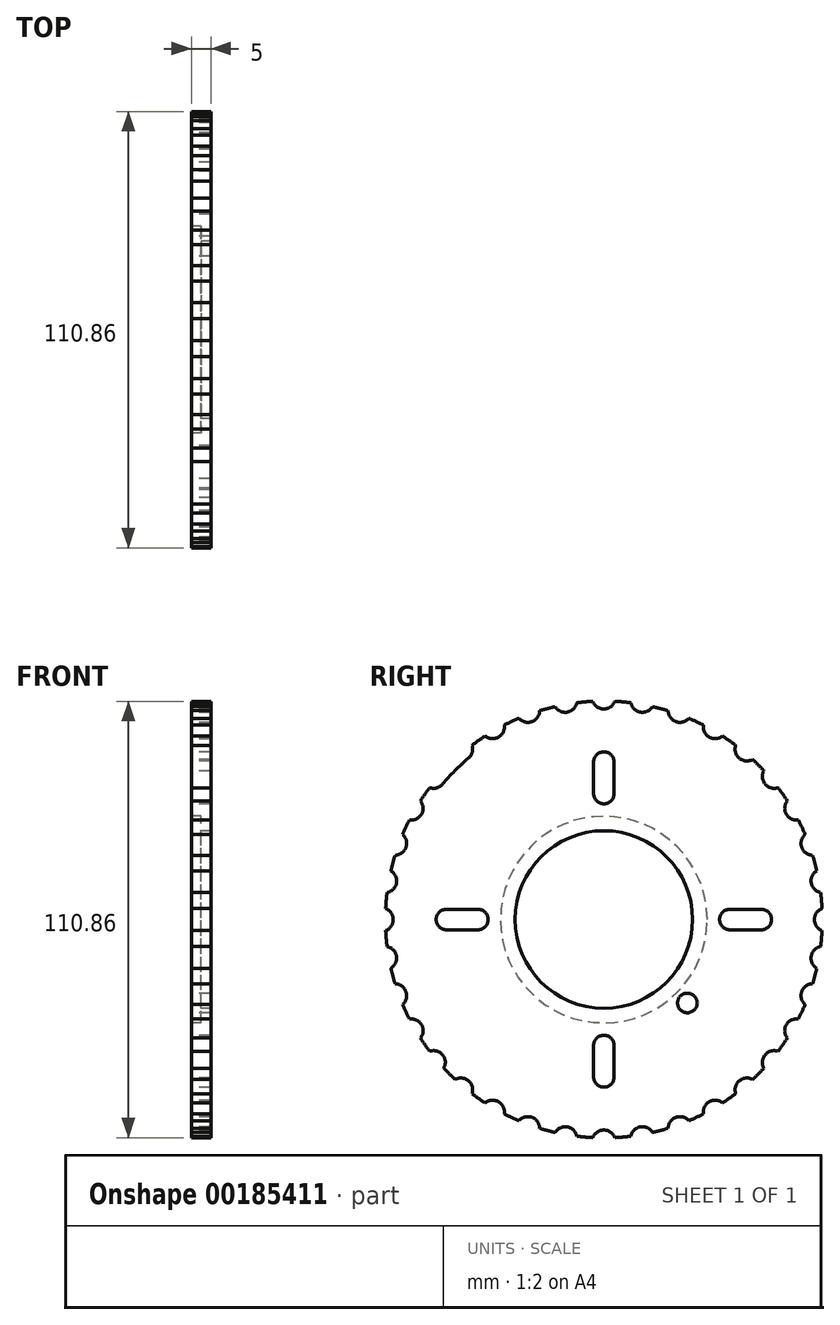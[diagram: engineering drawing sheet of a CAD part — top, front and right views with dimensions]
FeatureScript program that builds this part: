
annotation { "Feature Type Name" : "Feature", "Feature Type Description" : "" }
export const myFeature = defineFeature(function(context is Context, id is Id, definition is map)
    precondition{}
    {
        {
            var Q0;
            Q0=qCreatedBy(makeId("Right.planeOp"),FACE);
            var sketch = newSketch(context, id + "F0", { "sketchPlane" : qUnion([Q0])});
            skCircle(sketch, "E0", {"center": v(0, 0) * mm, "radius": 26.25 * mm});
            skCircle(sketch, "E1", {"center": v(0, 0) * mm, "radius": 22.55 * mm});
            skLineSegment(sketch, "E2", {"start": v(0, 6.12) * mm, "end": v(0, -11) * mm, "construction": true});
            skLineSegment(sketch, "E3", {"start": v(0, 40) * mm, "end": v(0, 32) * mm, "construction": true});
            skArc(sketch, "E4.0.startCap", {"start": v(-2.6, 40) * mm, "mid": v(0, 42.6) * mm, "end": v(2.6, 40) * mm});
            skArc(sketch, "E4.0.endCap", {"start": v(2.6, 32) * mm, "mid": v(0, 29.4) * mm, "end": v(-2.6, 32) * mm});
            skLineSegment(sketch, "E4.0.left", {"start": v(2.6, 40) * mm, "end": v(2.6, 32) * mm});
            skLineSegment(sketch, "E4.0.right", {"start": v(-2.6, 40) * mm, "end": v(-2.6, 32) * mm});
            skArc(sketch, "E5.1.0", {"start": v(-32, 2.6) * mm, "mid": v(-29.4, 0) * mm, "end": v(-32, -2.6) * mm});
            skLineSegment(sketch, "E5.1.1", {"start": v(-40, -2.6) * mm, "end": v(-32, -2.6) * mm});
            skLineSegment(sketch, "E5.1.2", {"start": v(-40, 2.6) * mm, "end": v(-32, 2.6) * mm});
            skArc(sketch, "E5.1.3", {"start": v(-40, -2.6) * mm, "mid": v(-42.6, 0) * mm, "end": v(-40, 2.6) * mm});
            skArc(sketch, "E5.2.0", {"start": v(-2.6, -32) * mm, "mid": v(0, -29.4) * mm, "end": v(2.6, -32) * mm});
            skLineSegment(sketch, "E5.2.1", {"start": v(2.6, -40) * mm, "end": v(2.6, -32) * mm});
            skLineSegment(sketch, "E5.2.2", {"start": v(-2.6, -40) * mm, "end": v(-2.6, -32) * mm});
            skArc(sketch, "E5.2.3", {"start": v(2.6, -40) * mm, "mid": v(0, -42.6) * mm, "end": v(-2.6, -40) * mm});
            skArc(sketch, "E5.3.0", {"start": v(32, -2.6) * mm, "mid": v(29.4, 0) * mm, "end": v(32, 2.6) * mm});
            skLineSegment(sketch, "E5.3.1", {"start": v(40, 2.6) * mm, "end": v(32, 2.6) * mm});
            skLineSegment(sketch, "E5.3.2", {"start": v(40, -2.6) * mm, "end": v(32, -2.6) * mm});
            skArc(sketch, "E5.3.3", {"start": v(40, 2.6) * mm, "mid": v(42.6, 0) * mm, "end": v(40, -2.6) * mm});
            skCircle(sketch, "E6", {"center": v(0, 0) * mm, "radius": 53.5 * mm});
            skArc(sketch, "E7", {"start": v(-2.8, 55.43) * mm, "mid": v(0, -55.5) * mm, "end": v(2.8, 55.43) * mm});
            skCircle(sketch, "E8", {"center": v(0, 0) * mm, "radius": 56.5 * mm, "construction": true});
            skArc(sketch, "E9", {"start": v(-2.8, 55.43) * mm, "mid": v(0, 53.5) * mm, "end": v(2.8, 55.43) * mm});
            skPoint(sketch, "E10.visualSharp", {"position": v(2.8, 55.43) * mm});
            skLineSegment(sketch, "E11", {"start": v(0, 0) * mm, "end": v(21.21, -21.21) * mm, "construction": true});
            skCircle(sketch, "E12", {"center": v(21.21, -21.21) * mm, "radius": 2.5 * mm});
            skArc(sketch, "E13.1.0", {"start": v(-12.38, 54.1) * mm, "mid": v(-9.3, 52.69) * mm, "end": v(-6.87, 55.07) * mm});
            skArc(sketch, "E13.2.0", {"start": v(-21.6, 51.13) * mm, "mid": v(-18.3, 50.27) * mm, "end": v(-16.32, 53.04) * mm});
            skArc(sketch, "E13.3.0", {"start": v(-30.14, 46.6) * mm, "mid": v(-26.75, 46.33) * mm, "end": v(-25.29, 49.4) * mm});
            skArc(sketch, "E13.4.0", {"start": v(-37.78, 40.66) * mm, "mid": v(-34.39, 40.98) * mm, "end": v(-33.48, 44.26) * mm});
            skArc(sketch, "E13.5.0", {"start": v(-44.26, 33.48) * mm, "mid": v(-40.98, 34.39) * mm, "end": v(-40.66, 37.78) * mm});
            skArc(sketch, "E13.6.0", {"start": v(-49.4, 25.29) * mm, "mid": v(-46.33, 26.75) * mm, "end": v(-46.6, 30.14) * mm});
            skArc(sketch, "E13.7.0", {"start": v(-53.04, 16.32) * mm, "mid": v(-50.27, 18.3) * mm, "end": v(-51.13, 21.6) * mm});
            skArc(sketch, "E13.8.0", {"start": v(-55.07, 6.87) * mm, "mid": v(-52.69, 9.3) * mm, "end": v(-54.1, 12.38) * mm});
            skArc(sketch, "E13.9.0", {"start": v(-55.43, -2.8) * mm, "mid": v(-53.5, 0) * mm, "end": v(-55.43, 2.8) * mm});
            skArc(sketch, "E13.10.0", {"start": v(-54.1, -12.38) * mm, "mid": v(-52.69, -9.3) * mm, "end": v(-55.07, -6.87) * mm});
            skArc(sketch, "E13.11.0", {"start": v(-51.13, -21.6) * mm, "mid": v(-50.27, -18.3) * mm, "end": v(-53.04, -16.32) * mm});
            skArc(sketch, "E13.12.0", {"start": v(-46.6, -30.14) * mm, "mid": v(-46.33, -26.75) * mm, "end": v(-49.4, -25.29) * mm});
            skArc(sketch, "E13.13.0", {"start": v(-40.66, -37.78) * mm, "mid": v(-40.98, -34.39) * mm, "end": v(-44.26, -33.48) * mm});
            skArc(sketch, "E13.14.0", {"start": v(-33.48, -44.26) * mm, "mid": v(-34.39, -40.98) * mm, "end": v(-37.78, -40.66) * mm});
            skArc(sketch, "E13.15.0", {"start": v(-25.29, -49.4) * mm, "mid": v(-26.75, -46.33) * mm, "end": v(-30.14, -46.6) * mm});
            skArc(sketch, "E13.16.0", {"start": v(-16.32, -53.04) * mm, "mid": v(-18.3, -50.27) * mm, "end": v(-21.6, -51.13) * mm});
            skArc(sketch, "E13.17.0", {"start": v(-6.87, -55.07) * mm, "mid": v(-9.3, -52.69) * mm, "end": v(-12.38, -54.1) * mm});
            skArc(sketch, "E13.18.0", {"start": v(2.8, -55.43) * mm, "mid": v(0, -53.5) * mm, "end": v(-2.8, -55.43) * mm});
            skArc(sketch, "E13.19.0", {"start": v(12.38, -54.1) * mm, "mid": v(9.3, -52.69) * mm, "end": v(6.87, -55.07) * mm});
            skArc(sketch, "E13.20.0", {"start": v(21.6, -51.13) * mm, "mid": v(18.3, -50.27) * mm, "end": v(16.32, -53.04) * mm});
            skArc(sketch, "E13.21.0", {"start": v(30.14, -46.6) * mm, "mid": v(26.75, -46.33) * mm, "end": v(25.29, -49.4) * mm});
            skArc(sketch, "E13.22.0", {"start": v(37.78, -40.66) * mm, "mid": v(34.39, -40.98) * mm, "end": v(33.48, -44.26) * mm});
            skArc(sketch, "E13.23.0", {"start": v(44.26, -33.48) * mm, "mid": v(40.98, -34.39) * mm, "end": v(40.66, -37.78) * mm});
            skArc(sketch, "E13.24.0", {"start": v(49.4, -25.29) * mm, "mid": v(46.33, -26.75) * mm, "end": v(46.6, -30.14) * mm});
            skArc(sketch, "E13.25.0", {"start": v(53.04, -16.32) * mm, "mid": v(50.27, -18.3) * mm, "end": v(51.13, -21.6) * mm});
            skArc(sketch, "E13.26.0", {"start": v(55.07, -6.87) * mm, "mid": v(52.69, -9.3) * mm, "end": v(54.1, -12.38) * mm});
            skArc(sketch, "E13.27.0", {"start": v(55.43, 2.8) * mm, "mid": v(53.5, 0) * mm, "end": v(55.43, -2.8) * mm});
            skArc(sketch, "E13.28.0", {"start": v(54.1, 12.38) * mm, "mid": v(52.69, 9.3) * mm, "end": v(55.07, 6.87) * mm});
            skArc(sketch, "E13.29.0", {"start": v(51.13, 21.6) * mm, "mid": v(50.27, 18.3) * mm, "end": v(53.04, 16.32) * mm});
            skArc(sketch, "E13.30.0", {"start": v(46.6, 30.14) * mm, "mid": v(46.33, 26.75) * mm, "end": v(49.4, 25.29) * mm});
            skArc(sketch, "E13.31.0", {"start": v(40.66, 37.78) * mm, "mid": v(40.98, 34.39) * mm, "end": v(44.26, 33.48) * mm});
            skArc(sketch, "E13.32.0", {"start": v(33.48, 44.26) * mm, "mid": v(34.39, 40.98) * mm, "end": v(37.78, 40.66) * mm});
            skArc(sketch, "E13.33.0", {"start": v(25.29, 49.4) * mm, "mid": v(26.75, 46.33) * mm, "end": v(30.14, 46.6) * mm});
            skArc(sketch, "E13.34.0", {"start": v(16.32, 53.04) * mm, "mid": v(18.3, 50.27) * mm, "end": v(21.6, 51.13) * mm});
            skArc(sketch, "E13.35.0", {"start": v(6.87, 55.07) * mm, "mid": v(9.3, 52.69) * mm, "end": v(12.38, 54.1) * mm});
            skSolve(sketch);
        }
        {
            var Q0;
            {var subQ0=sQuery(id+"F0.wireOp",EDGE,"E10.filletArc");Q0=makeQuery(id+"F0.imprint","IMPRINT",FACE,{"disambiguationData":[TD([[makeQuery(id+"F0.imprint","IMPRINT",EDGE,{"derivedFrom":subQ0}),1.0]])]});}
            var Q1;
            {var subQ0=sQuery(id+"F0.wireOp",EDGE,"af735512-6c5a-431f-a23e-76d62cfa44da.34.0");Q1=makeQuery(id+"F0.imprint","IMPRINT",FACE,{"disambiguationData":[TD([[makeQuery(id+"F0.imprint","IMPRINT",EDGE,{"derivedFrom":subQ0}),1.0]])]});}
            var Q2;
            {var subQ1=sQuery(id+"F0.wireOp",EDGE,"af735512-6c5a-431f-a23e-76d62cfa44da.33.0");Q2=makeQuery(id+"F0.imprint","IMPRINT",FACE,{"disambiguationData":[TD([[makeQuery(id+"F0.imprint","IMPRINT",EDGE,{"derivedFrom":subQ1}),1.0]])]});}
            var Q3;
            {var subQ1=sQuery(id+"F0.wireOp",EDGE,"af735512-6c5a-431f-a23e-76d62cfa44da.32.0");Q3=makeQuery(id+"F0.imprint","IMPRINT",FACE,{"disambiguationData":[TD([[makeQuery(id+"F0.imprint","IMPRINT",EDGE,{"derivedFrom":subQ1}),1.0]])]});}
            var Q4;
            {var subQ1=sQuery(id+"F0.wireOp",EDGE,"af735512-6c5a-431f-a23e-76d62cfa44da.31.0");Q4=makeQuery(id+"F0.imprint","IMPRINT",FACE,{"disambiguationData":[TD([[makeQuery(id+"F0.imprint","IMPRINT",EDGE,{"derivedFrom":subQ1}),1.0]])]});}
            var Q5;
            {var subQ1=sQuery(id+"F0.wireOp",EDGE,"af735512-6c5a-431f-a23e-76d62cfa44da.30.0");Q5=makeQuery(id+"F0.imprint","IMPRINT",FACE,{"disambiguationData":[TD([[makeQuery(id+"F0.imprint","IMPRINT",EDGE,{"derivedFrom":subQ1}),1.0]])]});}
            var Q6;
            {var subQ1=sQuery(id+"F0.wireOp",EDGE,"af735512-6c5a-431f-a23e-76d62cfa44da.29.0");Q6=makeQuery(id+"F0.imprint","IMPRINT",FACE,{"disambiguationData":[TD([[makeQuery(id+"F0.imprint","IMPRINT",EDGE,{"derivedFrom":subQ1}),1.0]])]});}
            var Q7;
            {var subQ1=sQuery(id+"F0.wireOp",EDGE,"af735512-6c5a-431f-a23e-76d62cfa44da.28.0");Q7=makeQuery(id+"F0.imprint","IMPRINT",FACE,{"disambiguationData":[TD([[makeQuery(id+"F0.imprint","IMPRINT",EDGE,{"derivedFrom":subQ1}),1.0]])]});}
            var Q8;
            {var subQ1=sQuery(id+"F0.wireOp",EDGE,"af735512-6c5a-431f-a23e-76d62cfa44da.27.0");Q8=makeQuery(id+"F0.imprint","IMPRINT",FACE,{"disambiguationData":[TD([[makeQuery(id+"F0.imprint","IMPRINT",EDGE,{"derivedFrom":subQ1}),1.0]])]});}
            var Q9;
            {var subQ0=sQuery(id+"F0.wireOp",EDGE,"af735512-6c5a-431f-a23e-76d62cfa44da.26.0");Q9=makeQuery(id+"F0.imprint","IMPRINT",FACE,{"disambiguationData":[TD([[makeQuery(id+"F0.imprint","IMPRINT",EDGE,{"derivedFrom":subQ0}),1.0]])]});}
            var Q10;
            {var subQ1=sQuery(id+"F0.wireOp",EDGE,"af735512-6c5a-431f-a23e-76d62cfa44da.25.0");Q10=makeQuery(id+"F0.imprint","IMPRINT",FACE,{"disambiguationData":[TD([[makeQuery(id+"F0.imprint","IMPRINT",EDGE,{"derivedFrom":subQ1}),1.0]])]});}
            var Q11;
            {var subQ0=sQuery(id+"F0.wireOp",EDGE,"af735512-6c5a-431f-a23e-76d62cfa44da.24.0");Q11=makeQuery(id+"F0.imprint","IMPRINT",FACE,{"disambiguationData":[TD([[makeQuery(id+"F0.imprint","IMPRINT",EDGE,{"derivedFrom":subQ0}),1.0]])]});}
            var Q12;
            {var subQ1=sQuery(id+"F0.wireOp",EDGE,"af735512-6c5a-431f-a23e-76d62cfa44da.23.0");Q12=makeQuery(id+"F0.imprint","IMPRINT",FACE,{"disambiguationData":[TD([[makeQuery(id+"F0.imprint","IMPRINT",EDGE,{"derivedFrom":subQ1}),1.0]])]});}
            var Q13;
            {var subQ1=sQuery(id+"F0.wireOp",EDGE,"af735512-6c5a-431f-a23e-76d62cfa44da.22.0");Q13=makeQuery(id+"F0.imprint","IMPRINT",FACE,{"disambiguationData":[TD([[makeQuery(id+"F0.imprint","IMPRINT",EDGE,{"derivedFrom":subQ1}),1.0]])]});}
            var Q14;
            {var subQ0=sQuery(id+"F0.wireOp",EDGE,"af735512-6c5a-431f-a23e-76d62cfa44da.21.0");Q14=makeQuery(id+"F0.imprint","IMPRINT",FACE,{"disambiguationData":[TD([[makeQuery(id+"F0.imprint","IMPRINT",EDGE,{"derivedFrom":subQ0}),1.0]])]});}
            var Q15;
            {var subQ1=sQuery(id+"F0.wireOp",EDGE,"af735512-6c5a-431f-a23e-76d62cfa44da.20.0");Q15=makeQuery(id+"F0.imprint","IMPRINT",FACE,{"disambiguationData":[TD([[makeQuery(id+"F0.imprint","IMPRINT",EDGE,{"derivedFrom":subQ1}),1.0]])]});}
            var Q16;
            {var subQ1=sQuery(id+"F0.wireOp",EDGE,"af735512-6c5a-431f-a23e-76d62cfa44da.19.0");Q16=makeQuery(id+"F0.imprint","IMPRINT",FACE,{"disambiguationData":[TD([[makeQuery(id+"F0.imprint","IMPRINT",EDGE,{"derivedFrom":subQ1}),1.0]])]});}
            var Q17;
            {var subQ0=sQuery(id+"F0.wireOp",EDGE,"af735512-6c5a-431f-a23e-76d62cfa44da.18.0");Q17=makeQuery(id+"F0.imprint","IMPRINT",FACE,{"disambiguationData":[TD([[makeQuery(id+"F0.imprint","IMPRINT",EDGE,{"derivedFrom":subQ0}),1.0]])]});}
            var Q18;
            {var subQ0=sQuery(id+"F0.wireOp",EDGE,"af735512-6c5a-431f-a23e-76d62cfa44da.17.0");Q18=makeQuery(id+"F0.imprint","IMPRINT",FACE,{"disambiguationData":[TD([[makeQuery(id+"F0.imprint","IMPRINT",EDGE,{"derivedFrom":subQ0}),1.0]])]});}
            var Q19;
            {var subQ0=sQuery(id+"F0.wireOp",EDGE,"af735512-6c5a-431f-a23e-76d62cfa44da.16.0");Q19=makeQuery(id+"F0.imprint","IMPRINT",FACE,{"disambiguationData":[TD([[makeQuery(id+"F0.imprint","IMPRINT",EDGE,{"derivedFrom":subQ0}),1.0]])]});}
            var Q20;
            {var subQ1=sQuery(id+"F0.wireOp",EDGE,"af735512-6c5a-431f-a23e-76d62cfa44da.15.0");Q20=makeQuery(id+"F0.imprint","IMPRINT",FACE,{"disambiguationData":[TD([[makeQuery(id+"F0.imprint","IMPRINT",EDGE,{"derivedFrom":subQ1}),1.0]])]});}
            var Q21;
            {var subQ1=sQuery(id+"F0.wireOp",EDGE,"af735512-6c5a-431f-a23e-76d62cfa44da.14.0");Q21=makeQuery(id+"F0.imprint","IMPRINT",FACE,{"disambiguationData":[TD([[makeQuery(id+"F0.imprint","IMPRINT",EDGE,{"derivedFrom":subQ1}),1.0]])]});}
            var Q22;
            {var subQ0=sQuery(id+"F0.wireOp",EDGE,"af735512-6c5a-431f-a23e-76d62cfa44da.13.0");Q22=makeQuery(id+"F0.imprint","IMPRINT",FACE,{"disambiguationData":[TD([[makeQuery(id+"F0.imprint","IMPRINT",EDGE,{"derivedFrom":subQ0}),1.0]])]});}
            var Q23;
            {var subQ1=sQuery(id+"F0.wireOp",EDGE,"af735512-6c5a-431f-a23e-76d62cfa44da.12.0");Q23=makeQuery(id+"F0.imprint","IMPRINT",FACE,{"disambiguationData":[TD([[makeQuery(id+"F0.imprint","IMPRINT",EDGE,{"derivedFrom":subQ1}),1.0]])]});}
            var Q24;
            {var subQ1=sQuery(id+"F0.wireOp",EDGE,"af735512-6c5a-431f-a23e-76d62cfa44da.11.0");Q24=makeQuery(id+"F0.imprint","IMPRINT",FACE,{"disambiguationData":[TD([[makeQuery(id+"F0.imprint","IMPRINT",EDGE,{"derivedFrom":subQ1}),1.0]])]});}
            var Q25;
            {var subQ1=sQuery(id+"F0.wireOp",EDGE,"af735512-6c5a-431f-a23e-76d62cfa44da.10.0");Q25=makeQuery(id+"F0.imprint","IMPRINT",FACE,{"disambiguationData":[TD([[makeQuery(id+"F0.imprint","IMPRINT",EDGE,{"derivedFrom":subQ1}),1.0]])]});}
            var Q26;
            {var subQ1=sQuery(id+"F0.wireOp",EDGE,"af735512-6c5a-431f-a23e-76d62cfa44da.9.0");Q26=makeQuery(id+"F0.imprint","IMPRINT",FACE,{"disambiguationData":[TD([[makeQuery(id+"F0.imprint","IMPRINT",EDGE,{"derivedFrom":subQ1}),1.0]])]});}
            var Q27;
            {var subQ1=sQuery(id+"F0.wireOp",EDGE,"af735512-6c5a-431f-a23e-76d62cfa44da.8.0");Q27=makeQuery(id+"F0.imprint","IMPRINT",FACE,{"disambiguationData":[TD([[makeQuery(id+"F0.imprint","IMPRINT",EDGE,{"derivedFrom":subQ1}),1.0]])]});}
            var Q28;
            {var subQ0=sQuery(id+"F0.wireOp",EDGE,"af735512-6c5a-431f-a23e-76d62cfa44da.7.0");Q28=makeQuery(id+"F0.imprint","IMPRINT",FACE,{"disambiguationData":[TD([[makeQuery(id+"F0.imprint","IMPRINT",EDGE,{"derivedFrom":subQ0}),1.0]])]});}
            var Q29;
            {var subQ1=sQuery(id+"F0.wireOp",EDGE,"af735512-6c5a-431f-a23e-76d62cfa44da.6.0");Q29=makeQuery(id+"F0.imprint","IMPRINT",FACE,{"disambiguationData":[TD([[makeQuery(id+"F0.imprint","IMPRINT",EDGE,{"derivedFrom":subQ1}),1.0]])]});}
            var Q30;
            {var subQ1=sQuery(id+"F0.wireOp",EDGE,"af735512-6c5a-431f-a23e-76d62cfa44da.5.0");Q30=makeQuery(id+"F0.imprint","IMPRINT",FACE,{"disambiguationData":[TD([[makeQuery(id+"F0.imprint","IMPRINT",EDGE,{"derivedFrom":subQ1}),1.0]])]});}
            var Q31;
            {var subQ1=sQuery(id+"F0.wireOp",EDGE,"af735512-6c5a-431f-a23e-76d62cfa44da.3.0");Q31=makeQuery(id+"F0.imprint","IMPRINT",FACE,{"disambiguationData":[TD([[makeQuery(id+"F0.imprint","IMPRINT",EDGE,{"derivedFrom":subQ1}),1.0]])]});}
            var Q32;
            {var subQ1=sQuery(id+"F0.wireOp",EDGE,"af735512-6c5a-431f-a23e-76d62cfa44da.2.0");Q32=makeQuery(id+"F0.imprint","IMPRINT",FACE,{"disambiguationData":[TD([[makeQuery(id+"F0.imprint","IMPRINT",EDGE,{"derivedFrom":subQ1}),1.0]])]});}
            var Q33;
            {var subQ1=sQuery(id+"F0.wireOp",EDGE,"af735512-6c5a-431f-a23e-76d62cfa44da.1.0");Q33=makeQuery(id+"F0.imprint","IMPRINT",FACE,{"disambiguationData":[TD([[makeQuery(id+"F0.imprint","IMPRINT",EDGE,{"derivedFrom":subQ1}),1.0]])]});}
            var Q34;
            {var subQ0=sQuery(id+"F0.wireOp",EDGE,"3b1b036c-b2a3-4702-b54c-793e93ef28af.filletArc");Q34=makeQuery(id+"F0.imprint","IMPRINT",FACE,{"disambiguationData":[TD([[makeQuery(id+"F0.imprint","IMPRINT",EDGE,{"derivedFrom":subQ0}),1.0]])]});}
            var Q35;
            {var subQ0=sQuery(id+"F0.wireOp",EDGE,"E9");var subQ1=sQuery(id+"F0.wireOp",EDGE,"E6");var subQ2=makeQuery(id+"F0.imprint","INTERSECT",VERTEX,{"derivedFrom":[subQ1,subQ0]});Q35=makeQuery(id+"F0.imprint","IMPRINT",FACE,{"disambiguationData":[TD([[makeQuery(id+"F0.imprint","IMPRINT",EDGE,{"disambiguationData":[TD([[subQ2,1.0]])],"derivedFrom":subQ1}),-1.0]])]});}
            var Q36;
            {var subQ0=sQuery(id+"F0.wireOp",EDGE,"E13.34.0");var subQ1=sQuery(id+"F0.wireOp",EDGE,"E6");var subQ2=makeQuery(id+"F0.imprint","INTERSECT",VERTEX,{"derivedFrom":[subQ1,subQ0]});Q36=makeQuery(id+"F0.imprint","IMPRINT",FACE,{"disambiguationData":[TD([[makeQuery(id+"F0.imprint","IMPRINT",EDGE,{"disambiguationData":[TD([[subQ2,-1.0]])],"derivedFrom":subQ1}),-1.0]])]});}
            var Q37;
            {var subQ0=sQuery(id+"F0.wireOp",EDGE,"E13.33.0");var subQ1=sQuery(id+"F0.wireOp",EDGE,"E6");var subQ2=makeQuery(id+"F0.imprint","INTERSECT",VERTEX,{"derivedFrom":[subQ1,subQ0]});Q37=makeQuery(id+"F0.imprint","IMPRINT",FACE,{"disambiguationData":[TD([[makeQuery(id+"F0.imprint","IMPRINT",EDGE,{"disambiguationData":[TD([[subQ2,-1.0]])],"derivedFrom":subQ1}),-1.0]])]});}
            var Q38;
            {var subQ0=sQuery(id+"F0.wireOp",EDGE,"E13.32.0");var subQ1=sQuery(id+"F0.wireOp",EDGE,"E6");var subQ2=makeQuery(id+"F0.imprint","INTERSECT",VERTEX,{"derivedFrom":[subQ1,subQ0]});Q38=makeQuery(id+"F0.imprint","IMPRINT",FACE,{"disambiguationData":[TD([[makeQuery(id+"F0.imprint","IMPRINT",EDGE,{"disambiguationData":[TD([[subQ2,-1.0]])],"derivedFrom":subQ1}),-1.0]])]});}
            var Q39;
            {var subQ0=sQuery(id+"F0.wireOp",EDGE,"E13.31.0");var subQ1=sQuery(id+"F0.wireOp",EDGE,"E6");var subQ2=makeQuery(id+"F0.imprint","INTERSECT",VERTEX,{"derivedFrom":[subQ1,subQ0]});Q39=makeQuery(id+"F0.imprint","IMPRINT",FACE,{"disambiguationData":[TD([[makeQuery(id+"F0.imprint","IMPRINT",EDGE,{"disambiguationData":[TD([[subQ2,-1.0]])],"derivedFrom":subQ1}),-1.0]])]});}
            var Q40;
            {var subQ0=sQuery(id+"F0.wireOp",EDGE,"E13.30.0");var subQ1=sQuery(id+"F0.wireOp",EDGE,"E6");var subQ2=makeQuery(id+"F0.imprint","INTERSECT",VERTEX,{"derivedFrom":[subQ1,subQ0]});Q40=makeQuery(id+"F0.imprint","IMPRINT",FACE,{"disambiguationData":[TD([[makeQuery(id+"F0.imprint","IMPRINT",EDGE,{"disambiguationData":[TD([[subQ2,-1.0]])],"derivedFrom":subQ1}),-1.0]])]});}
            var Q41;
            {var subQ0=sQuery(id+"F0.wireOp",EDGE,"E13.29.0");var subQ1=sQuery(id+"F0.wireOp",EDGE,"E6");var subQ2=makeQuery(id+"F0.imprint","INTERSECT",VERTEX,{"derivedFrom":[subQ1,subQ0]});Q41=makeQuery(id+"F0.imprint","IMPRINT",FACE,{"disambiguationData":[TD([[makeQuery(id+"F0.imprint","IMPRINT",EDGE,{"disambiguationData":[TD([[subQ2,-1.0]])],"derivedFrom":subQ1}),-1.0]])]});}
            var Q42;
            {var subQ0=sQuery(id+"F0.wireOp",EDGE,"E13.28.0");var subQ1=sQuery(id+"F0.wireOp",EDGE,"E6");var subQ2=makeQuery(id+"F0.imprint","INTERSECT",VERTEX,{"derivedFrom":[subQ1,subQ0]});Q42=makeQuery(id+"F0.imprint","IMPRINT",FACE,{"disambiguationData":[TD([[makeQuery(id+"F0.imprint","IMPRINT",EDGE,{"disambiguationData":[TD([[subQ2,-1.0]])],"derivedFrom":subQ1}),-1.0]])]});}
            var Q43;
            {var subQ0=sQuery(id+"F0.wireOp",EDGE,"E13.28.0");var subQ1=sQuery(id+"F0.wireOp",EDGE,"E6");var subQ2=makeQuery(id+"F0.imprint","INTERSECT",VERTEX,{"derivedFrom":[subQ1,subQ0]});Q43=makeQuery(id+"F0.imprint","IMPRINT",FACE,{"disambiguationData":[TD([[makeQuery(id+"F0.imprint","IMPRINT",EDGE,{"disambiguationData":[TD([[subQ2,1.0]])],"derivedFrom":subQ1}),-1.0]])]});}
            var Q44;
            {var subQ0=sQuery(id+"F0.wireOp",EDGE,"E13.27.0");var subQ1=sQuery(id+"F0.wireOp",EDGE,"E6");var subQ2=makeQuery(id+"F0.imprint","INTERSECT",VERTEX,{"derivedFrom":[subQ1,subQ0]});Q44=makeQuery(id+"F0.imprint","IMPRINT",FACE,{"disambiguationData":[TD([[makeQuery(id+"F0.imprint","IMPRINT",EDGE,{"disambiguationData":[TD([[subQ2,1.0]])],"derivedFrom":subQ1}),-1.0]])]});}
            var Q45;
            {var subQ0=sQuery(id+"F0.wireOp",EDGE,"E13.25.0");var subQ1=sQuery(id+"F0.wireOp",EDGE,"E6");var subQ2=makeQuery(id+"F0.imprint","INTERSECT",VERTEX,{"derivedFrom":[subQ1,subQ0]});Q45=makeQuery(id+"F0.imprint","IMPRINT",FACE,{"disambiguationData":[TD([[makeQuery(id+"F0.imprint","IMPRINT",EDGE,{"disambiguationData":[TD([[subQ2,-1.0]])],"derivedFrom":subQ1}),-1.0]])]});}
            var Q46;
            {var subQ0=sQuery(id+"F0.wireOp",EDGE,"E13.24.0");var subQ1=sQuery(id+"F0.wireOp",EDGE,"E6");var subQ2=makeQuery(id+"F0.imprint","INTERSECT",VERTEX,{"derivedFrom":[subQ1,subQ0]});Q46=makeQuery(id+"F0.imprint","IMPRINT",FACE,{"disambiguationData":[TD([[makeQuery(id+"F0.imprint","IMPRINT",EDGE,{"disambiguationData":[TD([[subQ2,-1.0]])],"derivedFrom":subQ1}),-1.0]])]});}
            var Q47;
            {var subQ0=sQuery(id+"F0.wireOp",EDGE,"E13.23.0");var subQ1=sQuery(id+"F0.wireOp",EDGE,"E6");var subQ2=makeQuery(id+"F0.imprint","INTERSECT",VERTEX,{"derivedFrom":[subQ1,subQ0]});Q47=makeQuery(id+"F0.imprint","IMPRINT",FACE,{"disambiguationData":[TD([[makeQuery(id+"F0.imprint","IMPRINT",EDGE,{"disambiguationData":[TD([[subQ2,-1.0]])],"derivedFrom":subQ1}),-1.0]])]});}
            var Q48;
            {var subQ0=sQuery(id+"F0.wireOp",EDGE,"E13.22.0");var subQ1=sQuery(id+"F0.wireOp",EDGE,"E6");var subQ2=makeQuery(id+"F0.imprint","INTERSECT",VERTEX,{"derivedFrom":[subQ1,subQ0]});Q48=makeQuery(id+"F0.imprint","IMPRINT",FACE,{"disambiguationData":[TD([[makeQuery(id+"F0.imprint","IMPRINT",EDGE,{"disambiguationData":[TD([[subQ2,-1.0]])],"derivedFrom":subQ1}),-1.0]])]});}
            var Q49;
            {var subQ0=sQuery(id+"F0.wireOp",EDGE,"E13.21.0");var subQ1=sQuery(id+"F0.wireOp",EDGE,"E6");var subQ2=makeQuery(id+"F0.imprint","INTERSECT",VERTEX,{"derivedFrom":[subQ1,subQ0]});Q49=makeQuery(id+"F0.imprint","IMPRINT",FACE,{"disambiguationData":[TD([[makeQuery(id+"F0.imprint","IMPRINT",EDGE,{"disambiguationData":[TD([[subQ2,-1.0]])],"derivedFrom":subQ1}),-1.0]])]});}
            var Q50;
            {var subQ0=sQuery(id+"F0.wireOp",EDGE,"E13.20.0");var subQ1=sQuery(id+"F0.wireOp",EDGE,"E6");var subQ2=makeQuery(id+"F0.imprint","INTERSECT",VERTEX,{"derivedFrom":[subQ1,subQ0]});Q50=makeQuery(id+"F0.imprint","IMPRINT",FACE,{"disambiguationData":[TD([[makeQuery(id+"F0.imprint","IMPRINT",EDGE,{"disambiguationData":[TD([[subQ2,-1.0]])],"derivedFrom":subQ1}),-1.0]])]});}
            var Q51;
            {var subQ0=sQuery(id+"F0.wireOp",EDGE,"E13.19.0");var subQ1=sQuery(id+"F0.wireOp",EDGE,"E6");var subQ2=makeQuery(id+"F0.imprint","INTERSECT",VERTEX,{"derivedFrom":[subQ1,subQ0]});Q51=makeQuery(id+"F0.imprint","IMPRINT",FACE,{"disambiguationData":[TD([[makeQuery(id+"F0.imprint","IMPRINT",EDGE,{"disambiguationData":[TD([[subQ2,-1.0]])],"derivedFrom":subQ1}),-1.0]])]});}
            var Q52;
            {var subQ0=sQuery(id+"F0.wireOp",EDGE,"E13.18.0");var subQ1=sQuery(id+"F0.wireOp",EDGE,"E6");var subQ2=makeQuery(id+"F0.imprint","INTERSECT",VERTEX,{"derivedFrom":[subQ1,subQ0]});Q52=makeQuery(id+"F0.imprint","IMPRINT",FACE,{"disambiguationData":[TD([[makeQuery(id+"F0.imprint","IMPRINT",EDGE,{"disambiguationData":[TD([[subQ2,-1.0]])],"derivedFrom":subQ1}),-1.0]])]});}
            var Q53;
            {var subQ0=sQuery(id+"F0.wireOp",EDGE,"E13.17.0");var subQ1=sQuery(id+"F0.wireOp",EDGE,"E6");var subQ2=makeQuery(id+"F0.imprint","INTERSECT",VERTEX,{"derivedFrom":[subQ1,subQ0]});Q53=makeQuery(id+"F0.imprint","IMPRINT",FACE,{"disambiguationData":[TD([[makeQuery(id+"F0.imprint","IMPRINT",EDGE,{"disambiguationData":[TD([[subQ2,-1.0]])],"derivedFrom":subQ1}),-1.0]])]});}
            var Q54;
            {var subQ0=sQuery(id+"F0.wireOp",EDGE,"E13.16.0");var subQ1=sQuery(id+"F0.wireOp",EDGE,"E6");var subQ2=makeQuery(id+"F0.imprint","INTERSECT",VERTEX,{"derivedFrom":[subQ1,subQ0]});Q54=makeQuery(id+"F0.imprint","IMPRINT",FACE,{"disambiguationData":[TD([[makeQuery(id+"F0.imprint","IMPRINT",EDGE,{"disambiguationData":[TD([[subQ2,-1.0]])],"derivedFrom":subQ1}),-1.0]])]});}
            var Q55;
            {var subQ0=sQuery(id+"F0.wireOp",EDGE,"E13.15.0");var subQ1=sQuery(id+"F0.wireOp",EDGE,"E6");var subQ2=makeQuery(id+"F0.imprint","INTERSECT",VERTEX,{"derivedFrom":[subQ1,subQ0]});Q55=makeQuery(id+"F0.imprint","IMPRINT",FACE,{"disambiguationData":[TD([[makeQuery(id+"F0.imprint","IMPRINT",EDGE,{"disambiguationData":[TD([[subQ2,-1.0]])],"derivedFrom":subQ1}),-1.0]])]});}
            var Q56;
            {var subQ0=sQuery(id+"F0.wireOp",EDGE,"E13.14.0");var subQ1=sQuery(id+"F0.wireOp",EDGE,"E6");var subQ2=makeQuery(id+"F0.imprint","INTERSECT",VERTEX,{"derivedFrom":[subQ1,subQ0]});Q56=makeQuery(id+"F0.imprint","IMPRINT",FACE,{"disambiguationData":[TD([[makeQuery(id+"F0.imprint","IMPRINT",EDGE,{"disambiguationData":[TD([[subQ2,-1.0]])],"derivedFrom":subQ1}),-1.0]])]});}
            var Q57;
            {var subQ0=sQuery(id+"F0.wireOp",EDGE,"E13.13.0");var subQ1=sQuery(id+"F0.wireOp",EDGE,"E6");var subQ2=makeQuery(id+"F0.imprint","INTERSECT",VERTEX,{"derivedFrom":[subQ1,subQ0]});Q57=makeQuery(id+"F0.imprint","IMPRINT",FACE,{"disambiguationData":[TD([[makeQuery(id+"F0.imprint","IMPRINT",EDGE,{"disambiguationData":[TD([[subQ2,-1.0]])],"derivedFrom":subQ1}),-1.0]])]});}
            var Q58;
            {var subQ0=sQuery(id+"F0.wireOp",EDGE,"E13.12.0");var subQ1=sQuery(id+"F0.wireOp",EDGE,"E6");var subQ2=makeQuery(id+"F0.imprint","INTERSECT",VERTEX,{"derivedFrom":[subQ1,subQ0]});Q58=makeQuery(id+"F0.imprint","IMPRINT",FACE,{"disambiguationData":[TD([[makeQuery(id+"F0.imprint","IMPRINT",EDGE,{"disambiguationData":[TD([[subQ2,-1.0]])],"derivedFrom":subQ1}),-1.0]])]});}
            var Q59;
            {var subQ0=sQuery(id+"F0.wireOp",EDGE,"E13.11.0");var subQ1=sQuery(id+"F0.wireOp",EDGE,"E6");var subQ2=makeQuery(id+"F0.imprint","INTERSECT",VERTEX,{"derivedFrom":[subQ1,subQ0]});Q59=makeQuery(id+"F0.imprint","IMPRINT",FACE,{"disambiguationData":[TD([[makeQuery(id+"F0.imprint","IMPRINT",EDGE,{"disambiguationData":[TD([[subQ2,-1.0]])],"derivedFrom":subQ1}),-1.0]])]});}
            var Q60;
            {var subQ0=sQuery(id+"F0.wireOp",EDGE,"E13.10.0");var subQ1=sQuery(id+"F0.wireOp",EDGE,"E6");var subQ2=makeQuery(id+"F0.imprint","INTERSECT",VERTEX,{"derivedFrom":[subQ1,subQ0]});Q60=makeQuery(id+"F0.imprint","IMPRINT",FACE,{"disambiguationData":[TD([[makeQuery(id+"F0.imprint","IMPRINT",EDGE,{"disambiguationData":[TD([[subQ2,-1.0]])],"derivedFrom":subQ1}),-1.0]])]});}
            var Q61;
            {var subQ0=sQuery(id+"F0.wireOp",EDGE,"E13.9.0");var subQ1=sQuery(id+"F0.wireOp",EDGE,"E6");var subQ2=makeQuery(id+"F0.imprint","INTERSECT",VERTEX,{"derivedFrom":[subQ1,subQ0]});Q61=makeQuery(id+"F0.imprint","IMPRINT",FACE,{"disambiguationData":[TD([[makeQuery(id+"F0.imprint","IMPRINT",EDGE,{"disambiguationData":[TD([[subQ2,-1.0]])],"derivedFrom":subQ1}),-1.0]])]});}
            var Q62;
            {var subQ0=sQuery(id+"F0.wireOp",EDGE,"E13.8.0");var subQ1=sQuery(id+"F0.wireOp",EDGE,"E6");var subQ2=makeQuery(id+"F0.imprint","INTERSECT",VERTEX,{"derivedFrom":[subQ1,subQ0]});Q62=makeQuery(id+"F0.imprint","IMPRINT",FACE,{"disambiguationData":[TD([[makeQuery(id+"F0.imprint","IMPRINT",EDGE,{"disambiguationData":[TD([[subQ2,-1.0]])],"derivedFrom":subQ1}),-1.0]])]});}
            var Q63;
            {var subQ0=sQuery(id+"F0.wireOp",EDGE,"E13.7.0");var subQ1=sQuery(id+"F0.wireOp",EDGE,"E6");var subQ2=makeQuery(id+"F0.imprint","INTERSECT",VERTEX,{"derivedFrom":[subQ1,subQ0]});Q63=makeQuery(id+"F0.imprint","IMPRINT",FACE,{"disambiguationData":[TD([[makeQuery(id+"F0.imprint","IMPRINT",EDGE,{"disambiguationData":[TD([[subQ2,-1.0]])],"derivedFrom":subQ1}),-1.0]])]});}
            var Q64;
            {var subQ0=sQuery(id+"F0.wireOp",EDGE,"E13.6.0");var subQ1=sQuery(id+"F0.wireOp",EDGE,"E6");var subQ2=makeQuery(id+"F0.imprint","INTERSECT",VERTEX,{"derivedFrom":[subQ1,subQ0]});Q64=makeQuery(id+"F0.imprint","IMPRINT",FACE,{"disambiguationData":[TD([[makeQuery(id+"F0.imprint","IMPRINT",EDGE,{"disambiguationData":[TD([[subQ2,-1.0]])],"derivedFrom":subQ1}),-1.0]])]});}
            var Q65;
            {var subQ0=sQuery(id+"F0.wireOp",EDGE,"E13.5.0");var subQ1=sQuery(id+"F0.wireOp",EDGE,"E6");var subQ2=makeQuery(id+"F0.imprint","INTERSECT",VERTEX,{"derivedFrom":[subQ1,subQ0]});Q65=makeQuery(id+"F0.imprint","IMPRINT",FACE,{"disambiguationData":[TD([[makeQuery(id+"F0.imprint","IMPRINT",EDGE,{"disambiguationData":[TD([[subQ2,-1.0]])],"derivedFrom":subQ1}),-1.0]])]});}
            var Q66;
            {var subQ0=sQuery(id+"F0.wireOp",EDGE,"E13.3.0");var subQ1=sQuery(id+"F0.wireOp",EDGE,"E6");var subQ2=makeQuery(id+"F0.imprint","INTERSECT",VERTEX,{"derivedFrom":[subQ1,subQ0]});Q66=makeQuery(id+"F0.imprint","IMPRINT",FACE,{"disambiguationData":[TD([[makeQuery(id+"F0.imprint","IMPRINT",EDGE,{"disambiguationData":[TD([[subQ2,-1.0]])],"derivedFrom":subQ1}),-1.0]])]});}
            var Q67;
            {var subQ0=sQuery(id+"F0.wireOp",EDGE,"E13.2.0");var subQ1=sQuery(id+"F0.wireOp",EDGE,"E6");var subQ2=makeQuery(id+"F0.imprint","INTERSECT",VERTEX,{"derivedFrom":[subQ1,subQ0]});Q67=makeQuery(id+"F0.imprint","IMPRINT",FACE,{"disambiguationData":[TD([[makeQuery(id+"F0.imprint","IMPRINT",EDGE,{"disambiguationData":[TD([[subQ2,-1.0]])],"derivedFrom":subQ1}),-1.0]])]});}
            var Q68;
            Q68=makeQuery(id+"F0.imprint","IMPRINT",FACE,{"disambiguationData":[TD([[makeQuery(id+"F0.imprint","IMPRINT",EDGE,{"derivedFrom":sQuery(id+"F0.wireOp",EDGE,"E0")}),-1.0]])]});
            var Q69;
            {var subQ0=sQuery(id+"F0.wireOp",EDGE,"E13.1.0");var subQ1=sQuery(id+"F0.wireOp",EDGE,"E6");var subQ2=makeQuery(id+"F0.imprint","INTERSECT",VERTEX,{"derivedFrom":[subQ1,subQ0]});Q69=makeQuery(id+"F0.imprint","IMPRINT",FACE,{"disambiguationData":[TD([[makeQuery(id+"F0.imprint","IMPRINT",EDGE,{"disambiguationData":[TD([[subQ2,-1.0]])],"derivedFrom":subQ1}),-1.0]])]});}
            var Q70;
            {var subQ0=sQuery(id+"F0.wireOp",EDGE,"E9");var subQ1=sQuery(id+"F0.wireOp",EDGE,"E6");var subQ2=makeQuery(id+"F0.imprint","INTERSECT",VERTEX,{"derivedFrom":[subQ1,subQ0]});Q70=makeQuery(id+"F0.imprint","IMPRINT",FACE,{"disambiguationData":[TD([[makeQuery(id+"F0.imprint","IMPRINT",EDGE,{"disambiguationData":[TD([[subQ2,-1.0]])],"derivedFrom":subQ1}),-1.0]])]});}
            extrude(context, id + "F2", {"entities" : qUnion([Q0, Q1, Q2, Q3, Q4, Q5, Q6, Q7, Q8, Q9, Q10, Q11, Q12, Q13, Q14, Q15, Q16, Q17, Q18, Q19, Q20, Q21, Q22, Q23, Q24, Q25, Q26, Q27, Q28, Q29, Q30, Q31, Q32, Q33, Q34, Q35, Q36, Q37, Q38, Q39, Q40, Q41, Q42, Q43, Q44, Q45, Q46, Q47, Q48, Q49, Q50, Q51, Q52, Q53, Q54, Q55, Q56, Q57, Q58, Q59, Q60, Q61, Q62, Q63, Q64, Q65, Q66, Q67, Q68, Q69, Q70]), "depth" : 5 * mm});
        }
        {
            var Q0;
            Q0=makeQuery(id+"F0.imprint","IMPRINT",FACE,{"disambiguationData":[TD([[makeQuery(id+"F0.imprint","IMPRINT",EDGE,{"derivedFrom":sQuery(id+"F0.wireOp",EDGE,"E0")}),1.0]])]});
            var Q1;
            Q1=makeQuery(id+"F2.opExtrude","CAP_FACE",FACE,{"disambiguationData":[OSD([sQuery(id+"F0.wireOp",EDGE,"E0"),sQuery(id+"F0.wireOp",EDGE,"E4.0.startCap"),sQuery(id+"F0.wireOp",EDGE,"E4.0.endCap"),sQuery(id+"F0.wireOp",EDGE,"E4.0.left"),sQuery(id+"F0.wireOp",EDGE,"E4.0.right"),sQuery(id+"F0.wireOp",EDGE,"E5.1.0"),sQuery(id+"F0.wireOp",EDGE,"E5.1.1"),sQuery(id+"F0.wireOp",EDGE,"E5.1.2"),sQuery(id+"F0.wireOp",EDGE,"E5.1.3"),sQuery(id+"F0.wireOp",EDGE,"E5.2.0"),sQuery(id+"F0.wireOp",EDGE,"E5.2.1"),sQuery(id+"F0.wireOp",EDGE,"E5.2.2"),sQuery(id+"F0.wireOp",EDGE,"E5.2.3"),sQuery(id+"F0.wireOp",EDGE,"E5.3.0"),sQuery(id+"F0.wireOp",EDGE,"E5.3.1"),sQuery(id+"F0.wireOp",EDGE,"E5.3.2"),sQuery(id+"F0.wireOp",EDGE,"E5.3.3"),sQuery(id+"F0.wireOp",EDGE,"E6"),sQuery(id+"F0.wireOp",EDGE,"E7"),sQuery(id+"F0.wireOp",EDGE,"E9"),sQuery(id+"F0.wireOp",EDGE,"E10.filletArc"),sQuery(id+"F0.wireOp",EDGE,"af735512-6c5a-431f-a23e-76d62cfa44da.1.0"),sQuery(id+"F0.wireOp",EDGE,"af735512-6c5a-431f-a23e-76d62cfa44da.1.1"),sQuery(id+"F0.wireOp",EDGE,"af735512-6c5a-431f-a23e-76d62cfa44da.2.0"),sQuery(id+"F0.wireOp",EDGE,"af735512-6c5a-431f-a23e-76d62cfa44da.2.1"),sQuery(id+"F0.wireOp",EDGE,"af735512-6c5a-431f-a23e-76d62cfa44da.2.2"),sQuery(id+"F0.wireOp",EDGE,"af735512-6c5a-431f-a23e-76d62cfa44da.3.0"),sQuery(id+"F0.wireOp",EDGE,"af735512-6c5a-431f-a23e-76d62cfa44da.3.1"),sQuery(id+"F0.wireOp",EDGE,"af735512-6c5a-431f-a23e-76d62cfa44da.3.2"),sQuery(id+"F0.wireOp",EDGE,"af735512-6c5a-431f-a23e-76d62cfa44da.4.0"),sQuery(id+"F0.wireOp",EDGE,"af735512-6c5a-431f-a23e-76d62cfa44da.4.1"),sQuery(id+"F0.wireOp",EDGE,"af735512-6c5a-431f-a23e-76d62cfa44da.4.2"),sQuery(id+"F0.wireOp",EDGE,"af735512-6c5a-431f-a23e-76d62cfa44da.5.0"),sQuery(id+"F0.wireOp",EDGE,"af735512-6c5a-431f-a23e-76d62cfa44da.5.1"),sQuery(id+"F0.wireOp",EDGE,"af735512-6c5a-431f-a23e-76d62cfa44da.5.2"),sQuery(id+"F0.wireOp",EDGE,"af735512-6c5a-431f-a23e-76d62cfa44da.6.0"),sQuery(id+"F0.wireOp",EDGE,"af735512-6c5a-431f-a23e-76d62cfa44da.6.1"),sQuery(id+"F0.wireOp",EDGE,"af735512-6c5a-431f-a23e-76d62cfa44da.6.2"),sQuery(id+"F0.wireOp",EDGE,"af735512-6c5a-431f-a23e-76d62cfa44da.7.0"),sQuery(id+"F0.wireOp",EDGE,"af735512-6c5a-431f-a23e-76d62cfa44da.7.1"),sQuery(id+"F0.wireOp",EDGE,"af735512-6c5a-431f-a23e-76d62cfa44da.7.2"),sQuery(id+"F0.wireOp",EDGE,"af735512-6c5a-431f-a23e-76d62cfa44da.8.0"),sQuery(id+"F0.wireOp",EDGE,"af735512-6c5a-431f-a23e-76d62cfa44da.8.1"),sQuery(id+"F0.wireOp",EDGE,"af735512-6c5a-431f-a23e-76d62cfa44da.8.2"),sQuery(id+"F0.wireOp",EDGE,"af735512-6c5a-431f-a23e-76d62cfa44da.9.0"),sQuery(id+"F0.wireOp",EDGE,"af735512-6c5a-431f-a23e-76d62cfa44da.9.1"),sQuery(id+"F0.wireOp",EDGE,"af735512-6c5a-431f-a23e-76d62cfa44da.9.2"),sQuery(id+"F0.wireOp",EDGE,"af735512-6c5a-431f-a23e-76d62cfa44da.10.0"),sQuery(id+"F0.wireOp",EDGE,"af735512-6c5a-431f-a23e-76d62cfa44da.10.1"),sQuery(id+"F0.wireOp",EDGE,"af735512-6c5a-431f-a23e-76d62cfa44da.10.2"),sQuery(id+"F0.wireOp",EDGE,"af735512-6c5a-431f-a23e-76d62cfa44da.11.0"),sQuery(id+"F0.wireOp",EDGE,"af735512-6c5a-431f-a23e-76d62cfa44da.11.1"),sQuery(id+"F0.wireOp",EDGE,"af735512-6c5a-431f-a23e-76d62cfa44da.11.2"),sQuery(id+"F0.wireOp",EDGE,"af735512-6c5a-431f-a23e-76d62cfa44da.12.0"),sQuery(id+"F0.wireOp",EDGE,"af735512-6c5a-431f-a23e-76d62cfa44da.12.1"),sQuery(id+"F0.wireOp",EDGE,"af735512-6c5a-431f-a23e-76d62cfa44da.12.2"),sQuery(id+"F0.wireOp",EDGE,"af735512-6c5a-431f-a23e-76d62cfa44da.13.0"),sQuery(id+"F0.wireOp",EDGE,"af735512-6c5a-431f-a23e-76d62cfa44da.13.1"),sQuery(id+"F0.wireOp",EDGE,"af735512-6c5a-431f-a23e-76d62cfa44da.13.2"),sQuery(id+"F0.wireOp",EDGE,"af735512-6c5a-431f-a23e-76d62cfa44da.14.0"),sQuery(id+"F0.wireOp",EDGE,"af735512-6c5a-431f-a23e-76d62cfa44da.14.1"),sQuery(id+"F0.wireOp",EDGE,"af735512-6c5a-431f-a23e-76d62cfa44da.14.2"),sQuery(id+"F0.wireOp",EDGE,"af735512-6c5a-431f-a23e-76d62cfa44da.15.0"),sQuery(id+"F0.wireOp",EDGE,"af735512-6c5a-431f-a23e-76d62cfa44da.15.1"),sQuery(id+"F0.wireOp",EDGE,"af735512-6c5a-431f-a23e-76d62cfa44da.15.2"),sQuery(id+"F0.wireOp",EDGE,"af735512-6c5a-431f-a23e-76d62cfa44da.16.0"),sQuery(id+"F0.wireOp",EDGE,"af735512-6c5a-431f-a23e-76d62cfa44da.16.1"),sQuery(id+"F0.wireOp",EDGE,"af735512-6c5a-431f-a23e-76d62cfa44da.16.2"),sQuery(id+"F0.wireOp",EDGE,"af735512-6c5a-431f-a23e-76d62cfa44da.17.0"),sQuery(id+"F0.wireOp",EDGE,"af735512-6c5a-431f-a23e-76d62cfa44da.17.1"),sQuery(id+"F0.wireOp",EDGE,"af735512-6c5a-431f-a23e-76d62cfa44da.17.2"),sQuery(id+"F0.wireOp",EDGE,"af735512-6c5a-431f-a23e-76d62cfa44da.18.0"),sQuery(id+"F0.wireOp",EDGE,"af735512-6c5a-431f-a23e-76d62cfa44da.18.1"),sQuery(id+"F0.wireOp",EDGE,"af735512-6c5a-431f-a23e-76d62cfa44da.18.2"),sQuery(id+"F0.wireOp",EDGE,"af735512-6c5a-431f-a23e-76d62cfa44da.19.0"),sQuery(id+"F0.wireOp",EDGE,"af735512-6c5a-431f-a23e-76d62cfa44da.19.1"),sQuery(id+"F0.wireOp",EDGE,"af735512-6c5a-431f-a23e-76d62cfa44da.19.2"),sQuery(id+"F0.wireOp",EDGE,"af735512-6c5a-431f-a23e-76d62cfa44da.20.0"),sQuery(id+"F0.wireOp",EDGE,"af735512-6c5a-431f-a23e-76d62cfa44da.20.1"),sQuery(id+"F0.wireOp",EDGE,"af735512-6c5a-431f-a23e-76d62cfa44da.20.2"),sQuery(id+"F0.wireOp",EDGE,"af735512-6c5a-431f-a23e-76d62cfa44da.21.0"),sQuery(id+"F0.wireOp",EDGE,"af735512-6c5a-431f-a23e-76d62cfa44da.21.1"),sQuery(id+"F0.wireOp",EDGE,"af735512-6c5a-431f-a23e-76d62cfa44da.21.2"),sQuery(id+"F0.wireOp",EDGE,"af735512-6c5a-431f-a23e-76d62cfa44da.22.0"),sQuery(id+"F0.wireOp",EDGE,"af735512-6c5a-431f-a23e-76d62cfa44da.22.1"),sQuery(id+"F0.wireOp",EDGE,"af735512-6c5a-431f-a23e-76d62cfa44da.22.2"),sQuery(id+"F0.wireOp",EDGE,"af735512-6c5a-431f-a23e-76d62cfa44da.23.0"),sQuery(id+"F0.wireOp",EDGE,"af735512-6c5a-431f-a23e-76d62cfa44da.23.1"),sQuery(id+"F0.wireOp",EDGE,"af735512-6c5a-431f-a23e-76d62cfa44da.23.2"),sQuery(id+"F0.wireOp",EDGE,"af735512-6c5a-431f-a23e-76d62cfa44da.24.0"),sQuery(id+"F0.wireOp",EDGE,"af735512-6c5a-431f-a23e-76d62cfa44da.24.1"),sQuery(id+"F0.wireOp",EDGE,"af735512-6c5a-431f-a23e-76d62cfa44da.24.2"),sQuery(id+"F0.wireOp",EDGE,"af735512-6c5a-431f-a23e-76d62cfa44da.25.0"),sQuery(id+"F0.wireOp",EDGE,"af735512-6c5a-431f-a23e-76d62cfa44da.25.1"),sQuery(id+"F0.wireOp",EDGE,"af735512-6c5a-431f-a23e-76d62cfa44da.25.2"),sQuery(id+"F0.wireOp",EDGE,"af735512-6c5a-431f-a23e-76d62cfa44da.26.0"),sQuery(id+"F0.wireOp",EDGE,"af735512-6c5a-431f-a23e-76d62cfa44da.26.1"),sQuery(id+"F0.wireOp",EDGE,"af735512-6c5a-431f-a23e-76d62cfa44da.26.2"),sQuery(id+"F0.wireOp",EDGE,"af735512-6c5a-431f-a23e-76d62cfa44da.27.0"),sQuery(id+"F0.wireOp",EDGE,"af735512-6c5a-431f-a23e-76d62cfa44da.27.1"),sQuery(id+"F0.wireOp",EDGE,"af735512-6c5a-431f-a23e-76d62cfa44da.27.2"),sQuery(id+"F0.wireOp",EDGE,"af735512-6c5a-431f-a23e-76d62cfa44da.28.0"),sQuery(id+"F0.wireOp",EDGE,"af735512-6c5a-431f-a23e-76d62cfa44da.28.1"),sQuery(id+"F0.wireOp",EDGE,"af735512-6c5a-431f-a23e-76d62cfa44da.28.2"),sQuery(id+"F0.wireOp",EDGE,"af735512-6c5a-431f-a23e-76d62cfa44da.29.0"),sQuery(id+"F0.wireOp",EDGE,"af735512-6c5a-431f-a23e-76d62cfa44da.29.1"),sQuery(id+"F0.wireOp",EDGE,"af735512-6c5a-431f-a23e-76d62cfa44da.29.2"),sQuery(id+"F0.wireOp",EDGE,"af735512-6c5a-431f-a23e-76d62cfa44da.30.0"),sQuery(id+"F0.wireOp",EDGE,"af735512-6c5a-431f-a23e-76d62cfa44da.30.1"),sQuery(id+"F0.wireOp",EDGE,"af735512-6c5a-431f-a23e-76d62cfa44da.30.2"),sQuery(id+"F0.wireOp",EDGE,"af735512-6c5a-431f-a23e-76d62cfa44da.31.0"),sQuery(id+"F0.wireOp",EDGE,"af735512-6c5a-431f-a23e-76d62cfa44da.31.1"),sQuery(id+"F0.wireOp",EDGE,"af735512-6c5a-431f-a23e-76d62cfa44da.31.2"),sQuery(id+"F0.wireOp",EDGE,"af735512-6c5a-431f-a23e-76d62cfa44da.32.0"),sQuery(id+"F0.wireOp",EDGE,"af735512-6c5a-431f-a23e-76d62cfa44da.32.1"),sQuery(id+"F0.wireOp",EDGE,"af735512-6c5a-431f-a23e-76d62cfa44da.32.2"),sQuery(id+"F0.wireOp",EDGE,"af735512-6c5a-431f-a23e-76d62cfa44da.33.0"),sQuery(id+"F0.wireOp",EDGE,"af735512-6c5a-431f-a23e-76d62cfa44da.33.1"),sQuery(id+"F0.wireOp",EDGE,"af735512-6c5a-431f-a23e-76d62cfa44da.33.2"),sQuery(id+"F0.wireOp",EDGE,"af735512-6c5a-431f-a23e-76d62cfa44da.34.0"),sQuery(id+"F0.wireOp",EDGE,"af735512-6c5a-431f-a23e-76d62cfa44da.34.1"),sQuery(id+"F0.wireOp",EDGE,"af735512-6c5a-431f-a23e-76d62cfa44da.34.2"),sQuery(id+"F0.wireOp",EDGE,"af735512-6c5a-431f-a23e-76d62cfa44da.35.0"),sQuery(id+"F0.wireOp",EDGE,"af735512-6c5a-431f-a23e-76d62cfa44da.35.1"),sQuery(id+"F0.wireOp",EDGE,"af735512-6c5a-431f-a23e-76d62cfa44da.35.2"),sQuery(id+"F0.wireOp",EDGE,"E12")])],"isStart":false});
            var Q2;
            Q2=makeQuery(id+"F2.opExtrude","CAP_FACE",FACE,{"disambiguationData":[OSD([sQuery(id+"FhzCYWocmGlqY3F1R_0.wireOp",EDGE,"a90b205b-c74d-458f-a1b6-75efac5bb8c1"),sQuery(id+"FhzCYWocmGlqY3F1R_0.wireOp",EDGE,"5210f86f-b657-47b3-b8af-156fb96cf149"),sQuery(id+"FhzCYWocmGlqY3F1R_0.wireOp",EDGE,"5c9960c7-659c-4360-9ed4-8d801816f910"),sQuery(id+"FhzCYWocmGlqY3F1R_0.wireOp",EDGE,"3d91fcf1-d09f-4f6b-b63e-741f8d8d2bcb"),sQuery(id+"FhzCYWocmGlqY3F1R_0.wireOp",EDGE,"f47fae6e-29df-449b-bb2a-ad06100ca350.1.0"),sQuery(id+"FhzCYWocmGlqY3F1R_0.wireOp",EDGE,"f47fae6e-29df-449b-bb2a-ad06100ca350.2.0"),sQuery(id+"FhzCYWocmGlqY3F1R_0.wireOp",EDGE,"f47fae6e-29df-449b-bb2a-ad06100ca350.3.0"),sQuery(id+"FhzCYWocmGlqY3F1R_0.wireOp",EDGE,"7beaed13-4a19-4201-8461-04744382ca8b.filletArc"),sQuery(id+"FhzCYWocmGlqY3F1R_0.wireOp",EDGE,"1e98ad8c-ee3f-4189-87f3-318f96d909ee.filletArc"),sQuery(id+"FhzCYWocmGlqY3F1R_0.wireOp",EDGE,"2d9fc021-5b0f-499c-bc6b-b3291faaa8a8"),sQuery(id+"FhzCYWocmGlqY3F1R_0.wireOp",EDGE,"8c08c8ae-3611-4956-8b58-36fd99375acd.2.0"),sQuery(id+"FhzCYWocmGlqY3F1R_0.wireOp",EDGE,"8c08c8ae-3611-4956-8b58-36fd99375acd.2.1"),sQuery(id+"FhzCYWocmGlqY3F1R_0.wireOp",EDGE,"8c08c8ae-3611-4956-8b58-36fd99375acd.2.2"),sQuery(id+"FhzCYWocmGlqY3F1R_0.wireOp",EDGE,"8c08c8ae-3611-4956-8b58-36fd99375acd.3.0"),sQuery(id+"FhzCYWocmGlqY3F1R_0.wireOp",EDGE,"8c08c8ae-3611-4956-8b58-36fd99375acd.3.1"),sQuery(id+"FhzCYWocmGlqY3F1R_0.wireOp",EDGE,"8c08c8ae-3611-4956-8b58-36fd99375acd.3.2"),sQuery(id+"FhzCYWocmGlqY3F1R_0.wireOp",EDGE,"8c08c8ae-3611-4956-8b58-36fd99375acd.4.0"),sQuery(id+"FhzCYWocmGlqY3F1R_0.wireOp",EDGE,"8c08c8ae-3611-4956-8b58-36fd99375acd.4.1"),sQuery(id+"FhzCYWocmGlqY3F1R_0.wireOp",EDGE,"8c08c8ae-3611-4956-8b58-36fd99375acd.4.2"),sQuery(id+"FhzCYWocmGlqY3F1R_0.wireOp",EDGE,"8c08c8ae-3611-4956-8b58-36fd99375acd.5.0"),sQuery(id+"FhzCYWocmGlqY3F1R_0.wireOp",EDGE,"8c08c8ae-3611-4956-8b58-36fd99375acd.5.1"),sQuery(id+"FhzCYWocmGlqY3F1R_0.wireOp",EDGE,"8c08c8ae-3611-4956-8b58-36fd99375acd.5.2"),sQuery(id+"FhzCYWocmGlqY3F1R_0.wireOp",EDGE,"8c08c8ae-3611-4956-8b58-36fd99375acd.6.0"),sQuery(id+"FhzCYWocmGlqY3F1R_0.wireOp",EDGE,"8c08c8ae-3611-4956-8b58-36fd99375acd.6.1"),sQuery(id+"FhzCYWocmGlqY3F1R_0.wireOp",EDGE,"8c08c8ae-3611-4956-8b58-36fd99375acd.6.2"),sQuery(id+"FhzCYWocmGlqY3F1R_0.wireOp",EDGE,"8c08c8ae-3611-4956-8b58-36fd99375acd.7.0"),sQuery(id+"FhzCYWocmGlqY3F1R_0.wireOp",EDGE,"8c08c8ae-3611-4956-8b58-36fd99375acd.7.1"),sQuery(id+"FhzCYWocmGlqY3F1R_0.wireOp",EDGE,"8c08c8ae-3611-4956-8b58-36fd99375acd.7.2"),sQuery(id+"FhzCYWocmGlqY3F1R_0.wireOp",EDGE,"8c08c8ae-3611-4956-8b58-36fd99375acd.8.0"),sQuery(id+"FhzCYWocmGlqY3F1R_0.wireOp",EDGE,"8c08c8ae-3611-4956-8b58-36fd99375acd.8.1"),sQuery(id+"FhzCYWocmGlqY3F1R_0.wireOp",EDGE,"8c08c8ae-3611-4956-8b58-36fd99375acd.8.2"),sQuery(id+"FhzCYWocmGlqY3F1R_0.wireOp",EDGE,"8c08c8ae-3611-4956-8b58-36fd99375acd.9.0"),sQuery(id+"FhzCYWocmGlqY3F1R_0.wireOp",EDGE,"8c08c8ae-3611-4956-8b58-36fd99375acd.9.1"),sQuery(id+"FhzCYWocmGlqY3F1R_0.wireOp",EDGE,"8c08c8ae-3611-4956-8b58-36fd99375acd.9.2"),sQuery(id+"FhzCYWocmGlqY3F1R_0.wireOp",EDGE,"8c08c8ae-3611-4956-8b58-36fd99375acd.10.0"),sQuery(id+"FhzCYWocmGlqY3F1R_0.wireOp",EDGE,"8c08c8ae-3611-4956-8b58-36fd99375acd.10.1"),sQuery(id+"FhzCYWocmGlqY3F1R_0.wireOp",EDGE,"8c08c8ae-3611-4956-8b58-36fd99375acd.10.2"),sQuery(id+"FhzCYWocmGlqY3F1R_0.wireOp",EDGE,"8c08c8ae-3611-4956-8b58-36fd99375acd.11.0"),sQuery(id+"FhzCYWocmGlqY3F1R_0.wireOp",EDGE,"8c08c8ae-3611-4956-8b58-36fd99375acd.11.1"),sQuery(id+"FhzCYWocmGlqY3F1R_0.wireOp",EDGE,"8c08c8ae-3611-4956-8b58-36fd99375acd.11.2")])],"isStart":false});
            extrude(context, id + "F1", {"entities" : qUnion([Q0]), "operationType" : NewBodyOperationType.ADD, "endBound" : BoundingType.UP_TO_SURFACE, "endBoundEntityFace" : qUnion([Q1]), "depth" : 2.5 * mm, "hasSecondDirection" : true, "secondDirectionOppositeDirection" : false, "secondDirectionBoundEntityFace" : qUnion([Q2]), "secondDirectionDepth" : 2.5 * mm});
        }
    });
